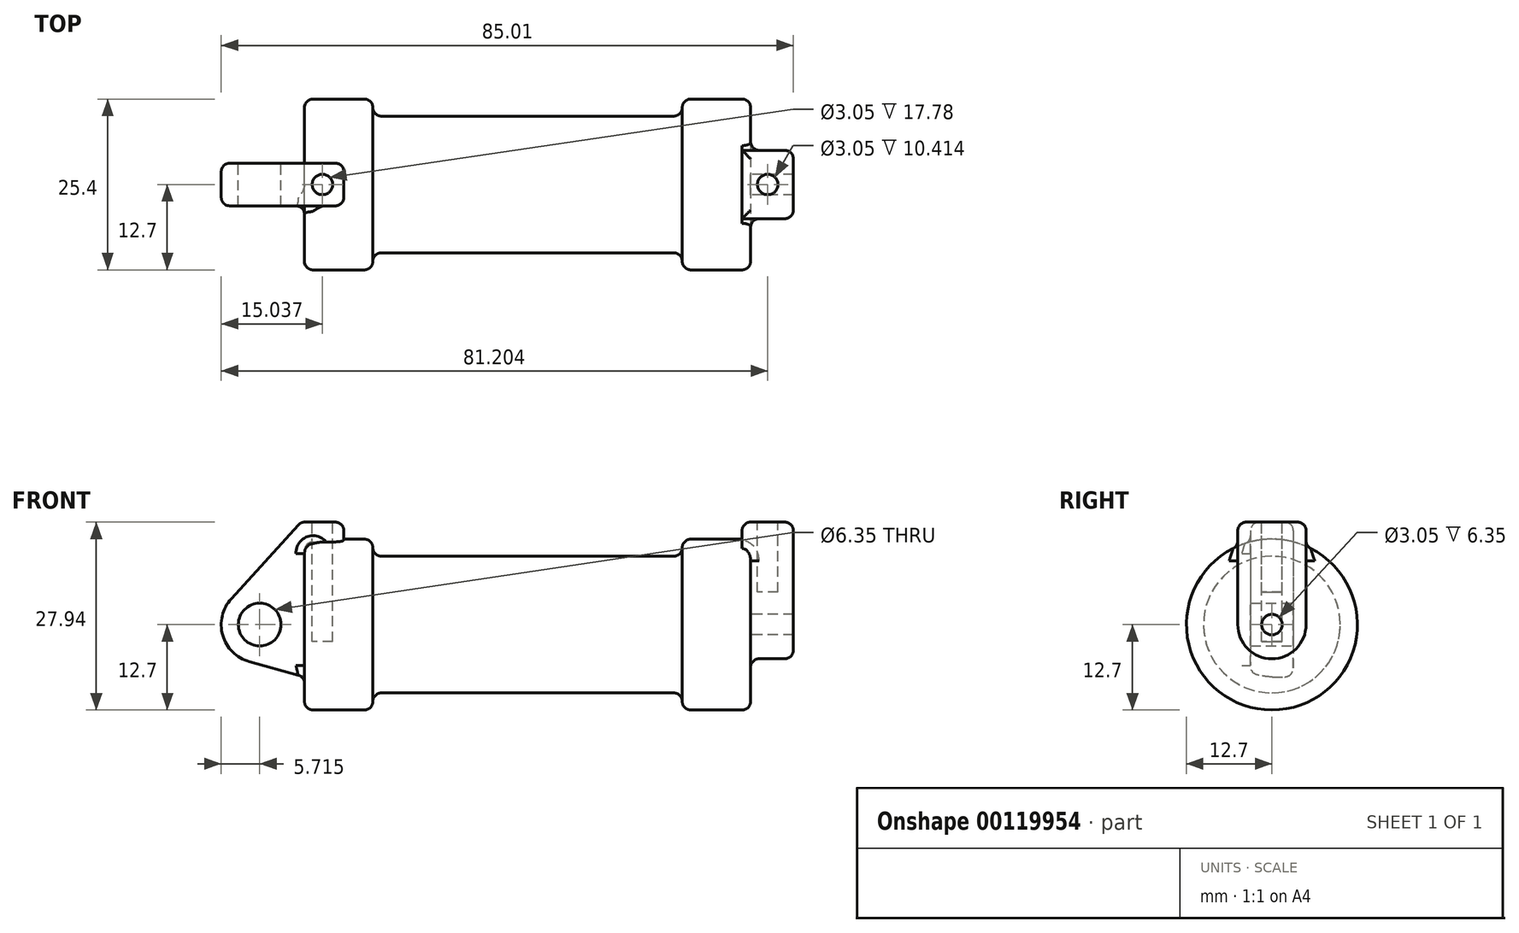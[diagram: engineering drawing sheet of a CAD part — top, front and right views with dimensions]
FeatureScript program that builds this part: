
annotation { "Feature Type Name" : "Feature", "Feature Type Description" : "" }
export const myFeature = defineFeature(function(context is Context, id is Id, definition is map)
    precondition{}
    {
        {
            var Q0;
            Q0=qCreatedBy(makeId("Front.planeOp"),FACE);
            var sketch = newSketch(context, id + "F0", { "sketchPlane" : qUnion([Q0])});
            skLineSegment(sketch, "E0", {"start": v(0, 0) * mm, "end": v(0, 12.7) * mm});
            skLineSegment(sketch, "E1", {"start": v(0, 12.7) * mm, "end": v(10.16, 12.7) * mm});
            skLineSegment(sketch, "E2", {"start": v(10.16, 12.7) * mm, "end": v(10.16, 10.16) * mm});
            skLineSegment(sketch, "E3", {"start": v(10.16, 10.16) * mm, "end": v(56.13, 10.16) * mm});
            skLineSegment(sketch, "E4", {"start": v(56.13, 10.16) * mm, "end": v(56.13, 12.7) * mm});
            skLineSegment(sketch, "E5", {"start": v(56.13, 12.7) * mm, "end": v(66.3, 12.7) * mm});
            skLineSegment(sketch, "E6", {"start": v(66.3, 12.7) * mm, "end": v(66.3, 0) * mm});
            skLineSegment(sketch, "E7", {"start": v(66.3, 0) * mm, "end": v(0, 0) * mm});
            skLineSegment(sketch, "E8", {"start": v(5.84, 15.24) * mm, "end": v(-0.5, 15.24) * mm});
            skLineSegment(sketch, "E9", {"start": v(-0.5, 15.24) * mm, "end": v(-10.88, 3.85) * mm});
            skLineSegment(sketch, "E10", {"start": v(0, 0) * mm, "end": v(-6.65, 0) * mm});
            skCircle(sketch, "E11", {"center": v(-6.65, 0) * mm, "radius": 5.72 * mm});
            skCircle(sketch, "E12", {"center": v(-6.65, 0) * mm, "radius": 3.18 * mm});
            skLineSegment(sketch, "E13", {"start": v(5.84, 15.24) * mm, "end": v(5.84, -9.4) * mm});
            skLineSegment(sketch, "E14", {"start": v(5.84, -9.4) * mm, "end": v(-8.18, -5.5) * mm});
            skSolve(sketch);
        }
        {
            var Q0;
            {var subQ0=sQuery(id+"F0.wireOp",EDGE,"E0");Q0=makeQuery(id+"F0.imprint","IMPRINT",FACE,{"disambiguationData":[TD([[makeQuery(id+"F0.imprint","IMPRINT",EDGE,{"derivedFrom":subQ0}),-1.0]])]});}
            var Q1;
            {var subQ0=sQuery(id+"F0.wireOp",EDGE,"E2");Q1=makeQuery(id+"F0.imprint","IMPRINT",FACE,{"disambiguationData":[TD([[makeQuery(id+"F0.imprint","IMPRINT",EDGE,{"derivedFrom":subQ0}),-1.0]])]});}
            var Q2;
            Q2=sQuery(id+"F0.wireOp",EDGE,"E7");
            revolve(context, id + "F1", {"entities" : qUnion([Q0, Q1]), "axis" : qUnion([Q2]), "revolveType" : RevolveType.FULL});
        }
        {
            var Q0;
            {var subQ3=sQuery(id+"F0.wireOp",EDGE,"E0");Q0=makeQuery(id+"F0.imprint","IMPRINT",FACE,{"disambiguationData":[TD([[makeQuery(id+"F0.imprint","IMPRINT",EDGE,{"derivedFrom":subQ3}),1.0]])]});}
            var Q1;
            {var subQ0=sQuery(id+"F0.wireOp",EDGE,"E0");Q1=makeQuery(id+"F0.imprint","IMPRINT",FACE,{"disambiguationData":[TD([[makeQuery(id+"F0.imprint","IMPRINT",EDGE,{"derivedFrom":subQ0}),-1.0]])]});}
            var Q2;
            {var subQ4=sQuery(id+"F0.wireOp",EDGE,"E12");Q2=makeQuery(id+"F0.imprint","IMPRINT",FACE,{"disambiguationData":[TD([[makeQuery(id+"F0.imprint","IMPRINT",EDGE,{"derivedFrom":subQ4}),-1.0]])]});}
            var Q3;
            {var subQ0=sQuery(id+"F0.wireOp",EDGE,"E14");Q3=makeQuery(id+"F0.imprint","IMPRINT",FACE,{"disambiguationData":[TD([[makeQuery(id+"F0.imprint","IMPRINT",EDGE,{"derivedFrom":subQ0}),-1.0]])]});}
            extrude(context, id + "F2", {"entities" : qUnion([Q0, Q1, Q2, Q3]), "operationType" : NewBodyOperationType.ADD, "endBound" : BoundingType.SYMMETRIC, "depth" : 6.35 * mm});
        }
        {
            var Q0;
            Q0=makeQuery(id+"F1.opRevolve","SWEPT_FACE",FACE,{"disambiguationData":[OSD([sQuery(id+"F0.wireOp",EDGE,"E6")])]});
            var sketch = newSketch(context, id + "F3", { "sketchPlane" : qUnion([Q0])});
            skCircle(sketch, "E15", {"center": v(0, 0) * mm, "radius": 1.52 * mm});
            skCircle(sketch, "E16", {"center": v(0, 0) * mm, "radius": 5.08 * mm});
            skLineSegment(sketch, "E17", {"start": v(5.08, 0) * mm, "end": v(5.08, 15.24) * mm});
            skLineSegment(sketch, "E18", {"start": v(5.08, 15.24) * mm, "end": v(-5.08, 15.24) * mm});
            skLineSegment(sketch, "E19", {"start": v(-5.08, 15.24) * mm, "end": v(-5.08, 0) * mm});
            skSolve(sketch);
        }
        {
            var Q0;
            Q0 = qSketchRegion(id + "F3", true);
            var Q1;
            Q1 = qSketchRegion(id + "F5", true);
            extrude(context, id + "F4", {"entities" : qUnion([Q0, Q1]), "operationType" : NewBodyOperationType.ADD, "depth" : 6.35 * mm, "hasSecondDirection" : true, "secondDirectionOppositeDirection" : true, "secondDirectionDepth" : 1.27 * mm});
        }
        {
            var Q0;
            Q0=makeQuery(id+"F2.opExtrude","SWEPT_FACE",FACE,{"disambiguationData":[OSD([sQuery(id+"F0.wireOp",EDGE,"E8")])]});
            var sketch = newSketch(context, id + "F5", { "sketchPlane" : qUnion([Q0])});
            skCircle(sketch, "E20", {"center": v(2.67, 0) * mm, "radius": 1.52 * mm});
            skPoint(sketch, "E20.centerSnap0", {"position": v(5.84, 0) * mm});
            skPoint(sketch, "E20.centerSnap1", {"position": v(2.67, 3.18) * mm});
            skCircle(sketch, "E21", {"center": v(68.83, 0) * mm, "radius": 1.52 * mm});
            skPoint(sketch, "E21.centerSnap0", {"position": v(72.64, 0) * mm});
            skPoint(sketch, "E21.centerSnap1", {"position": v(68.83, 5.08) * mm});
            skSolve(sketch);
        }
        {
            var Q0;
            Q0=makeQuery(id+"F5.imprint","IMPRINT",FACE,{"disambiguationData":[TD([[makeQuery(id+"F5.imprint","IMPRINT",EDGE,{"derivedFrom":sQuery(id+"F5.wireOp",EDGE,"E20")}),1.0]])]});
            var Q1;
            Q1=sQuery(id+"F5.wireOp",EDGE,"E21");
            extrude(context, id + "F6", {"entities" : qUnion([Q0]), "operationType" : NewBodyOperationType.REMOVE, "surfaceEntities" : qUnion([Q1]), "oppositeDirection" : true, "depth" : 17.78 * mm});
        }
        {
            var Q0;
            Q0=makeQuery(id+"F5.imprint","IMPRINT",FACE,{"disambiguationData":[TD([[makeQuery(id+"F5.imprint","IMPRINT",EDGE,{"derivedFrom":sQuery(id+"F5.wireOp",EDGE,"E21")}),1.0]])]});
            extrude(context, id + "F7", {"entities" : qUnion([Q0]), "operationType" : NewBodyOperationType.REMOVE, "oppositeDirection" : true, "depth" : 10.4 * mm});
        }
        {
            var Q0;
            Q0=makeQuery(id+"F1.opRevolve","SWEPT_FACE",FACE,{"disambiguationData":[OSD([sQuery(id+"F0.wireOp",EDGE,"E3")])]});
            var Q1;
            Q1=makeQuery(id+"F1.opRevolve","SWEPT_EDGE",EDGE,{"disambiguationData":[OSD([sQuery(id+"F0.wireOp",EDGE,"E4"),sQuery(id+"F0.wireOp",EDGE,"E5")])]});
            var Q2;
            Q2=makeQuery(id+"F1.opRevolve","SWEPT_EDGE",EDGE,{"disambiguationData":[OSD([sQuery(id+"F0.wireOp",EDGE,"E1"),sQuery(id+"F0.wireOp",EDGE,"E2")])]});
            var Q3;
            Q3=makeQuery(id+"F1.opRevolve","SWEPT_EDGE",EDGE,{"disambiguationData":[OSD([sQuery(id+"F0.wireOp",EDGE,"E0"),sQuery(id+"F0.wireOp",EDGE,"E1")])]});
            var Q4;
            Q4=makeQuery(id+"F2.boolean.opBoolean","INTERSECT",EDGE,{"derivedFrom":[makeQuery(id+"F1.opRevolve","SWEPT_FACE",FACE,{"disambiguationData":[OSD([sQuery(id+"F0.wireOp",EDGE,"E0")])]}),makeQuery(id+"F2.opExtrude","CAP_FACE",FACE,{"disambiguationData":[OSD([sQuery(id+"F0.wireOp",EDGE,"E8"),sQuery(id+"F0.wireOp",EDGE,"E9"),sQuery(id+"F0.wireOp",EDGE,"E11"),sQuery(id+"F0.wireOp",EDGE,"E12"),sQuery(id+"F0.wireOp",EDGE,"E13"),sQuery(id+"F0.wireOp",EDGE,"E14")])],"isStart":false})]});
            var Q5;
            Q5=makeQuery(id+"F2.opExtrude","CAP_EDGE",EDGE,{"disambiguationData":[OSD([sQuery(id+"F0.wireOp",EDGE,"E9")])],"isStart":false});
            var Q6;
            Q6=makeQuery(id+"F2.opExtrude","CAP_EDGE",EDGE,{"disambiguationData":[OSD([sQuery(id+"F0.wireOp",EDGE,"E8")])],"isStart":false});
            var Q7;
            Q7=makeQuery(id+"F2.opExtrude","CAP_EDGE",EDGE,{"disambiguationData":[OSD([sQuery(id+"F0.wireOp",EDGE,"E8")])],"isStart":true});
            var Q8;
            Q8=makeQuery(id+"F2.opExtrude","SWEPT_EDGE",EDGE,{"disambiguationData":[OSD([sQuery(id+"F0.wireOp",EDGE,"E8"),sQuery(id+"F0.wireOp",EDGE,"E13")])]});
            var Q9;
            Q9=makeQuery(id+"F2.opExtrude","CAP_EDGE",EDGE,{"disambiguationData":[OSD([sQuery(id+"F0.wireOp",EDGE,"E13")])],"isStart":false});
            var Q10;
            Q10=makeQuery(id+"F2.opExtrude","CAP_EDGE",EDGE,{"disambiguationData":[OSD([sQuery(id+"F0.wireOp",EDGE,"E9")])],"isStart":true});
            var Q11;
            Q11=makeQuery(id+"F2.opExtrude","CAP_EDGE",EDGE,{"disambiguationData":[OSD([sQuery(id+"F0.wireOp",EDGE,"E13")])],"isStart":true});
            var Q12;
            Q12=makeQuery(id+"F4.opExtrude","CAP_EDGE",EDGE,{"disambiguationData":[OSD([sQuery(id+"F3.wireOp",EDGE,"E19")])],"isStart":false});
            var Q13;
            Q13=makeQuery(id+"F1.opRevolve","SWEPT_EDGE",EDGE,{"disambiguationData":[OSD([sQuery(id+"F0.wireOp",EDGE,"E5"),sQuery(id+"F0.wireOp",EDGE,"E6")])]});
            var Q14;
            Q14=makeQuery(id+"F4.opExtrude","SWEPT_EDGE",EDGE,{"disambiguationData":[OSD([sQuery(id+"F3.wireOp",EDGE,"E18"),sQuery(id+"F3.wireOp",EDGE,"E19")])]});
            var Q15;
            Q15=makeQuery(id+"F4.opExtrude","CAP_EDGE",EDGE,{"disambiguationData":[OSD([sQuery(id+"F3.wireOp",EDGE,"E18")])],"isStart":false});
            var Q16;
            Q16=makeQuery(id+"F4.opExtrude","SWEPT_EDGE",EDGE,{"disambiguationData":[OSD([sQuery(id+"F3.wireOp",EDGE,"E17"),sQuery(id+"F3.wireOp",EDGE,"E18")])]});
            var Q17;
            Q17=makeQuery(id+"F4.opExtrude","CAP_EDGE",EDGE,{"disambiguationData":[OSD([sQuery(id+"F3.wireOp",EDGE,"E18")])],"isStart":true});
            var Q18;
            Q18=makeQuery(id+"F4.boolean.opBoolean","INTERSECT",EDGE,{"derivedFrom":[makeQuery(id+"F1.opRevolve","SWEPT_FACE",FACE,{"disambiguationData":[OSD([sQuery(id+"F0.wireOp",EDGE,"E6")])]}),makeQuery(id+"F4.opExtrude","SWEPT_FACE",FACE,{"disambiguationData":[OSD([sQuery(id+"F3.wireOp",EDGE,"E19")])]})]});
            var Q19;
            Q19=makeQuery(id+"F2.opExtrude","SWEPT_EDGE",EDGE,{"disambiguationData":[OSD([sQuery(id+"F0.wireOp",EDGE,"E8"),sQuery(id+"F0.wireOp",EDGE,"E9")])]});
            fillet(context, id + "F8", {"entities" : qUnion([Q0, Q1, Q2, Q3, Q4, Q5, Q6, Q7, Q8, Q9, Q10, Q11, Q12, Q13, Q14, Q15, Q16, Q17, Q18, Q19]), "radius" : 1.27 * mm, "tangentPropagation" : true, "allowEdgeOverflow" : false});
        }
    });
